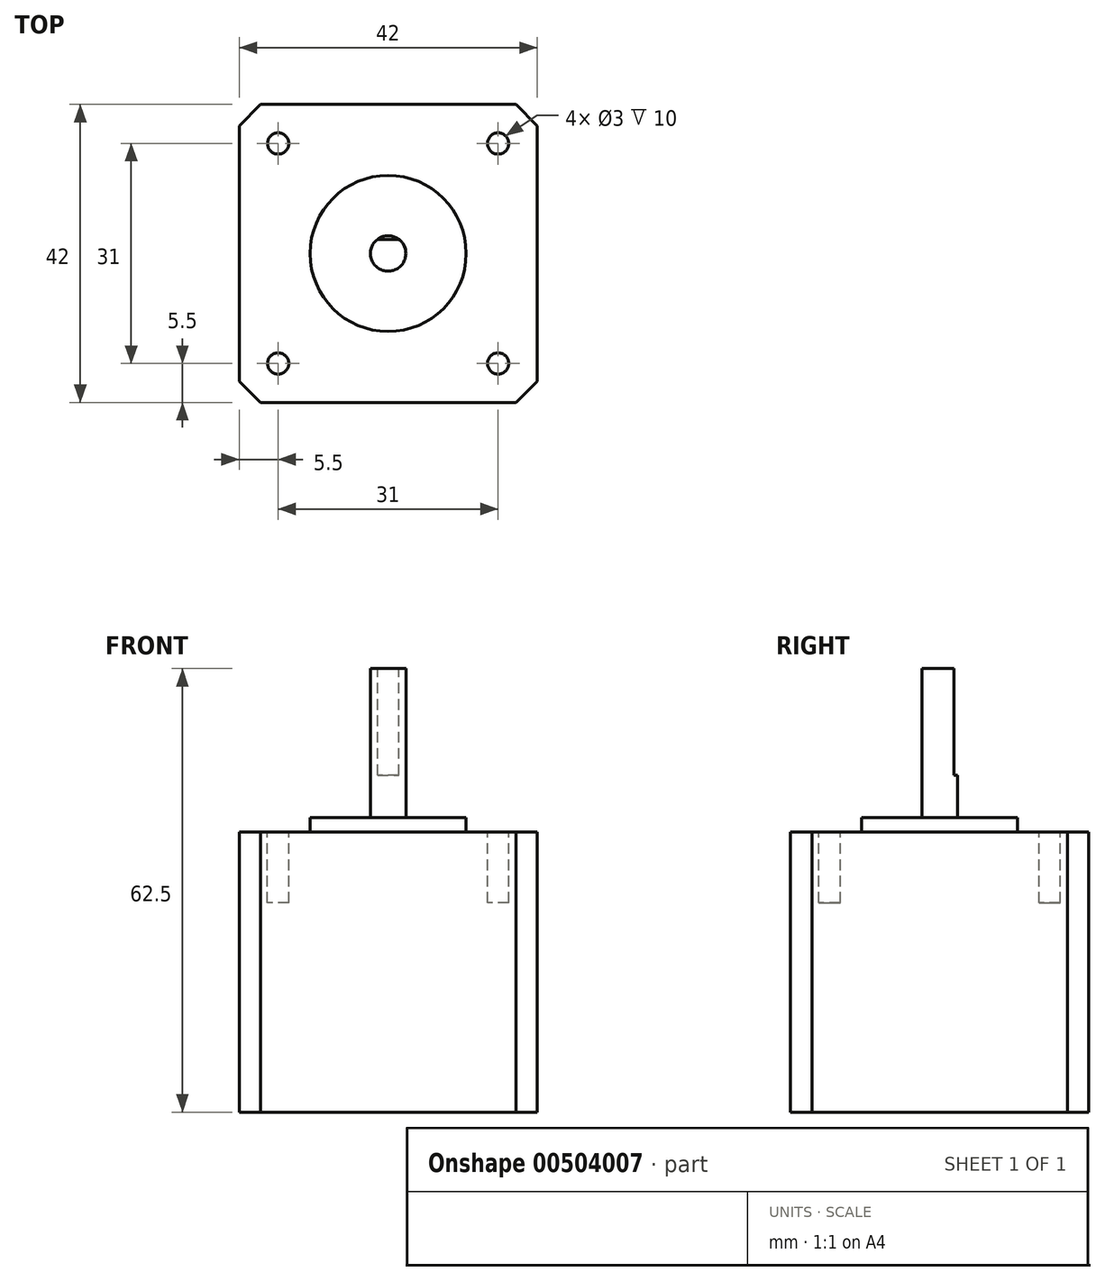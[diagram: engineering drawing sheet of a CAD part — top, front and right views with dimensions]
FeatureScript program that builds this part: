
annotation { "Feature Type Name" : "Feature", "Feature Type Description" : "" }
export const myFeature = defineFeature(function(context is Context, id is Id, definition is map)
    precondition{}
    {
        {
            var Q0;
            Q0=qCreatedBy(makeId("Top.planeOp"),FACE);
            var sketch = newSketch(context, id + "F0", { "sketchPlane" : qUnion([Q0])});
            skLineSegment(sketch, "E0.bottom", {"start": v(21, -21) * mm, "end": v(-21, -21) * mm});
            skLineSegment(sketch, "E0.top", {"start": v(21, 21) * mm, "end": v(-21, 21) * mm});
            skLineSegment(sketch, "E0.left", {"start": v(21, -21) * mm, "end": v(21, 21) * mm});
            skLineSegment(sketch, "E0.right", {"start": v(-21, -21) * mm, "end": v(-21, 21) * mm});
            skPoint(sketch, "E0.middle", {"position": v(0, 0) * mm});
            skSolve(sketch);
        }
        {
            var Q0;
            Q0=makeQuery(id+"F0.imprint","IMPRINT",FACE,{"disambiguationData":[TD([[makeQuery(id+"F0.imprint","IMPRINT",EDGE,{"derivedFrom":sQuery(id+"F0.wireOp",EDGE,"E0.bottom")}),-1.0]])]});
            extrude(context, id + "F1", {"entities" : qUnion([Q0]), "offsetDistance" : 25 * mm, "depth" : 39.5 * mm});
        }
        {
            var Q0;
            Q0=makeQuery(id+"F1.opExtrude","CAP_FACE",FACE,{"disambiguationData":[OSD([sQuery(id+"F0.wireOp",EDGE,"E0.bottom"),sQuery(id+"F0.wireOp",EDGE,"E0.top"),sQuery(id+"F0.wireOp",EDGE,"E0.left"),sQuery(id+"F0.wireOp",EDGE,"E0.right")])],"isStart":false});
            var sketch = newSketch(context, id + "F2", { "sketchPlane" : qUnion([Q0])});
            skLineSegment(sketch, "E1.bottom", {"start": v(15.5, 15.5) * mm, "end": v(-15.5, 15.5) * mm, "construction": true});
            skLineSegment(sketch, "E1.top", {"start": v(15.5, -15.5) * mm, "end": v(-15.5, -15.5) * mm, "construction": true});
            skLineSegment(sketch, "E1.left", {"start": v(15.5, 15.5) * mm, "end": v(15.5, -15.5) * mm, "construction": true});
            skLineSegment(sketch, "E1.right", {"start": v(-15.5, 15.5) * mm, "end": v(-15.5, -15.5) * mm, "construction": true});
            skPoint(sketch, "E1.middle", {"position": v(0, 0) * mm});
            skCircle(sketch, "E2", {"center": v(-15.5, 15.5) * mm, "radius": 1.5 * mm});
            skCircle(sketch, "E3", {"center": v(-15.5, -15.5) * mm, "radius": 1.5 * mm});
            skCircle(sketch, "E4", {"center": v(15.5, 15.5) * mm, "radius": 1.5 * mm});
            skCircle(sketch, "E5", {"center": v(15.5, -15.5) * mm, "radius": 1.5 * mm});
            skCircle(sketch, "E6", {"center": v(0, 0) * mm, "radius": 11 * mm});
            skSolve(sketch);
        }
        {
            var Q0;
            Q0=makeQuery(id+"F2.imprint","IMPRINT",FACE,{"disambiguationData":[TD([[makeQuery(id+"F2.imprint","IMPRINT",EDGE,{"derivedFrom":sQuery(id+"F2.wireOp",EDGE,"E3")}),1.0]])]});
            var Q1;
            Q1=makeQuery(id+"F2.imprint","IMPRINT",FACE,{"disambiguationData":[TD([[makeQuery(id+"F2.imprint","IMPRINT",EDGE,{"derivedFrom":sQuery(id+"F2.wireOp",EDGE,"E2")}),1.0]])]});
            var Q2;
            Q2=makeQuery(id+"F2.imprint","IMPRINT",FACE,{"disambiguationData":[TD([[makeQuery(id+"F2.imprint","IMPRINT",EDGE,{"derivedFrom":sQuery(id+"F2.wireOp",EDGE,"E4")}),1.0]])]});
            var Q3;
            Q3=makeQuery(id+"F2.imprint","IMPRINT",FACE,{"disambiguationData":[TD([[makeQuery(id+"F2.imprint","IMPRINT",EDGE,{"derivedFrom":sQuery(id+"F2.wireOp",EDGE,"E5")}),1.0]])]});
            var Q4;
            Q4=sQuery(id+"F2.wireOp",EDGE,"E2");
            var Q5;
            Q5=sQuery(id+"F2.wireOp",EDGE,"E3");
            var Q6;
            Q6=sQuery(id+"F2.wireOp",EDGE,"E5");
            var Q7;
            Q7=sQuery(id+"F2.wireOp",EDGE,"E4");
            extrude(context, id + "F3", {"entities" : qUnion([Q0, Q1, Q2, Q3]), "operationType" : NewBodyOperationType.REMOVE, "surfaceEntities" : qUnion([Q4, Q5, Q6, Q7]), "oppositeDirection" : true, "depth" : 10 * mm});
        }
        {
            var Q0;
            Q0=makeQuery(id+"F2.imprint","IMPRINT",FACE,{"disambiguationData":[TD([[makeQuery(id+"F2.imprint","IMPRINT",EDGE,{"derivedFrom":sQuery(id+"F2.wireOp",EDGE,"E6")}),1.0]])]});
            extrude(context, id + "F4", {"entities" : qUnion([Q0]), "operationType" : NewBodyOperationType.ADD, "depth" : 2 * mm});
        }
        {
            var Q0;
            Q0=makeQuery(id+"F4.opExtrude","CAP_FACE",FACE,{"disambiguationData":[OSD([sQuery(id+"F2.wireOp",EDGE,"E6")])],"isStart":false});
            var sketch = newSketch(context, id + "F5", { "sketchPlane" : qUnion([Q0])});
            skCircle(sketch, "E7", {"center": v(0, 0) * mm, "radius": 2.5 * mm});
            skSolve(sketch);
        }
        {
            var Q0;
            Q0=makeQuery(id+"F5.imprint","IMPRINT",FACE,{"disambiguationData":[TD([[makeQuery(id+"F5.imprint","IMPRINT",EDGE,{"derivedFrom":sQuery(id+"F5.wireOp",EDGE,"E7")}),1.0]])]});
            extrude(context, id + "F6", {"entities" : qUnion([Q0]), "operationType" : NewBodyOperationType.ADD, "offsetDistance" : 25 * mm, "depth" : 21 * mm});
        }
        {
            var Q0;
            Q0=makeQuery(id+"F6.opExtrude","CAP_FACE",FACE,{"disambiguationData":[OSD([sQuery(id+"F5.wireOp",EDGE,"E7")])],"isStart":false});
            var sketch = newSketch(context, id + "F7", { "sketchPlane" : qUnion([Q0])});
            skLineSegment(sketch, "E8", {"start": v(-1.5, 2) * mm, "end": v(1.5, 2) * mm});
            skSolve(sketch);
        }
        {
            var Q0;
            {var subQ0=sQuery(id+"F7.wireOp",EDGE,"E8");Q0=makeQuery(id+"F7.imprint","IMPRINT",FACE,{"disambiguationData":[TD([[makeQuery(id+"F7.imprint","IMPRINT",EDGE,{"derivedFrom":subQ0}),1.0]])]});}
            extrude(context, id + "F8", {"entities" : qUnion([Q0]), "operationType" : NewBodyOperationType.REMOVE, "oppositeDirection" : true, "depth" : 15 * mm});
        }
        {
            var Q0;
            Q0=makeQuery(id+"F1.opExtrude","SWEPT_EDGE",EDGE,{"disambiguationData":[OSD([sQuery(id+"F0.wireOp",EDGE,"E0.bottom"),sQuery(id+"F0.wireOp",EDGE,"E0.left")])]});
            var Q1;
            Q1=makeQuery(id+"F1.opExtrude","SWEPT_EDGE",EDGE,{"disambiguationData":[OSD([sQuery(id+"F0.wireOp",EDGE,"E0.top"),sQuery(id+"F0.wireOp",EDGE,"E0.left")])]});
            var Q2;
            Q2=makeQuery(id+"F1.opExtrude","SWEPT_EDGE",EDGE,{"disambiguationData":[OSD([sQuery(id+"F0.wireOp",EDGE,"E0.bottom"),sQuery(id+"F0.wireOp",EDGE,"E0.right")])]});
            var Q3;
            Q3=makeQuery(id+"F1.opExtrude","SWEPT_EDGE",EDGE,{"disambiguationData":[OSD([sQuery(id+"F0.wireOp",EDGE,"E0.top"),sQuery(id+"F0.wireOp",EDGE,"E0.right")])]});
            chamfer(context, id + "F9", {"entities" : qUnion([Q0, Q1, Q2, Q3]), "width" : 3 * mm, "tangentPropagation" : true});
        }
    });
